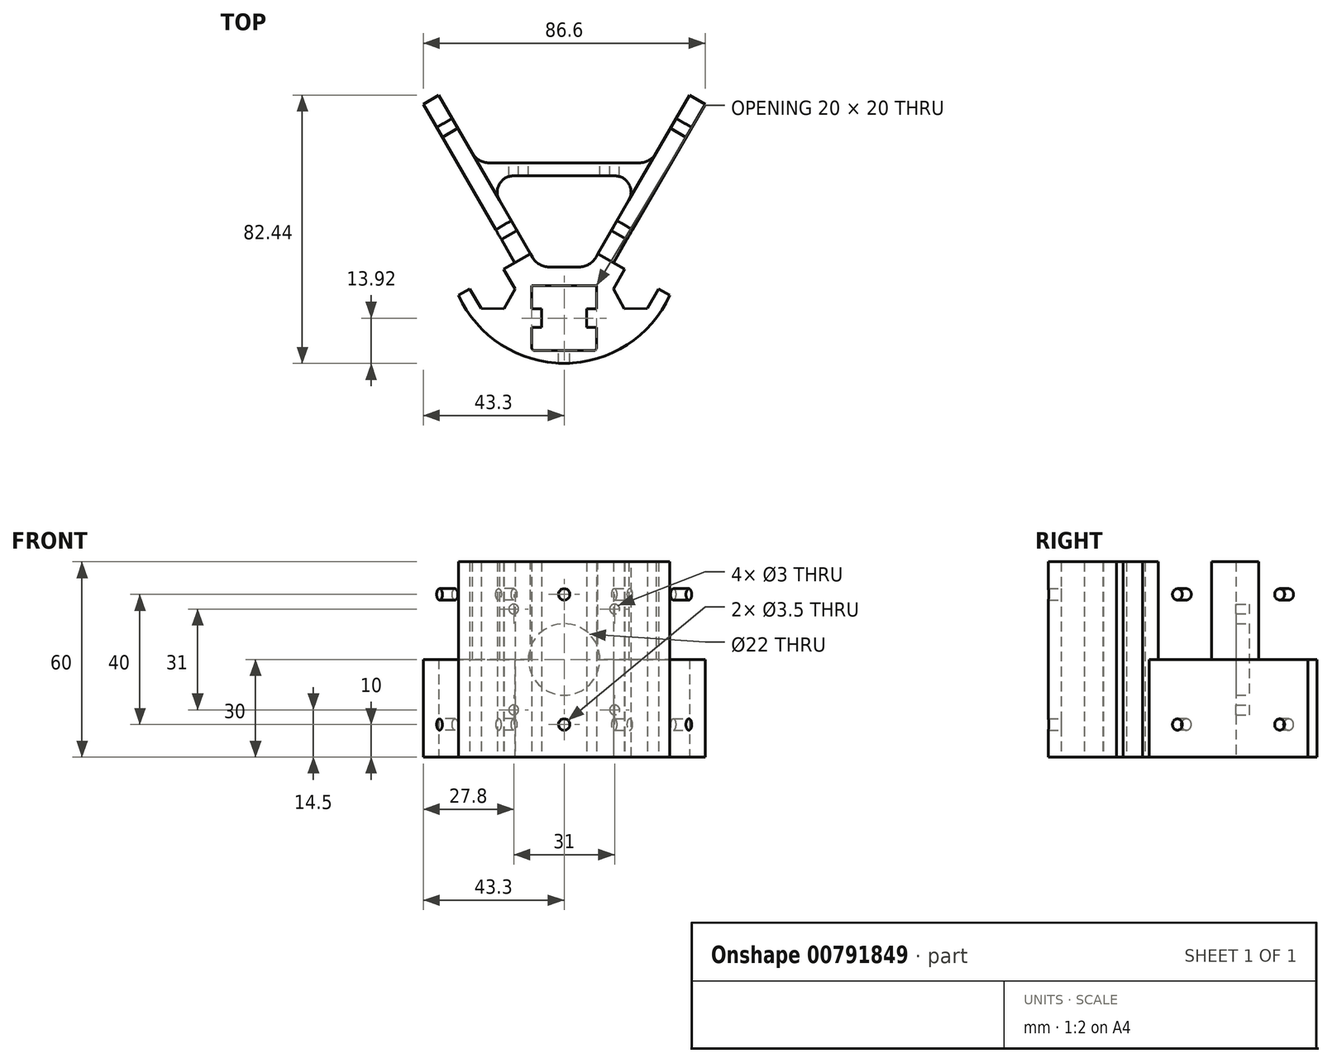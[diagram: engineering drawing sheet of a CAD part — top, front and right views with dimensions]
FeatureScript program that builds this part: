
annotation { "Feature Type Name" : "Feature", "Feature Type Description" : "" }
export const myFeature = defineFeature(function(context is Context, id is Id, definition is map)
    precondition{}
    {
        {
            var Q0;
            Q0=qCreatedBy(makeId("Top.planeOp"),FACE);
            var sketch = newSketch(context, id + "F0", { "sketchPlane" : qUnion([Q0])});
            skLineSegment(sketch, "E0", {"start": v(0, 0) * mm, "end": v(32.48, 0) * mm});
            skLineSegment(sketch, "E1", {"start": v(0, 0) * mm, "end": v(-32.48, 0) * mm});
            skArc(sketch, "E2", {"start": v(-32.48, 0) * mm, "mid": v(0, -20.94) * mm, "end": v(32.48, 0) * mm});
            skLineSegment(sketch, "E3", {"start": v(-32.48, 0) * mm, "end": v(-15.15, 10) * mm});
            skLineSegment(sketch, "E4", {"start": v(32.48, 0) * mm, "end": v(15.15, 10) * mm});
            skLineSegment(sketch, "E5", {"start": v(15.15, 10) * mm, "end": v(43.3, 58.75) * mm});
            skLineSegment(sketch, "E6", {"start": v(-15.15, 10) * mm, "end": v(-43.3, 58.75) * mm});
            skLineSegment(sketch, "E7", {"start": v(38.54, 61.5) * mm, "end": v(43.3, 58.75) * mm});
            skLineSegment(sketch, "E8.bottom", {"start": v(10, -17.02) * mm, "end": v(-10, -17.02) * mm});
            skLineSegment(sketch, "E8.top", {"start": v(10, 2.98) * mm, "end": v(-10, 2.98) * mm});
            skLineSegment(sketch, "E8.left", {"start": v(10, -17.02) * mm, "end": v(10, 2.98) * mm});
            skLineSegment(sketch, "E8.right", {"start": v(-10, -17.02) * mm, "end": v(-10, 2.98) * mm});
            skPoint(sketch, "E8.middle", {"position": v(0, -7.02) * mm});
            skLineSegment(sketch, "E9", {"start": v(-64.62, 8.7) * mm, "end": v(74.38, 8.7) * mm});
            skLineSegment(sketch, "E10", {"start": v(-43.3, 58.75) * mm, "end": v(-38.54, 61.5) * mm});
            skLineSegment(sketch, "E11", {"start": v(-38.54, 61.5) * mm, "end": v(-8.06, 8.7) * mm});
            skLineSegment(sketch, "E12", {"start": v(38.54, 61.5) * mm, "end": v(8.06, 8.7) * mm});
            skLineSegment(sketch, "E13", {"start": v(-64.62, 36.7) * mm, "end": v(67.86, 36.7) * mm});
            skLineSegment(sketch, "E14", {"start": v(-64.87, 40.7) * mm, "end": v(70.08, 40.7) * mm});
            skLineSegment(sketch, "E15.bottom", {"start": v(-10, -7.02) * mm, "end": v(-6.9, -7.02) * mm});
            skLineSegment(sketch, "E15.top", {"start": v(-10, -4.12) * mm, "end": v(-6.9, -4.12) * mm});
            skLineSegment(sketch, "E15.left", {"start": v(-10, -7.02) * mm, "end": v(-10, -4.12) * mm});
            skLineSegment(sketch, "E15.right", {"start": v(-6.9, -7.02) * mm, "end": v(-6.9, -4.12) * mm});
            skLineSegment(sketch, "E16.top", {"start": v(-10, -9.92) * mm, "end": v(-6.9, -9.92) * mm});
            skLineSegment(sketch, "E16.left", {"start": v(-10, -7.02) * mm, "end": v(-10, -9.92) * mm});
            skLineSegment(sketch, "E16.right", {"start": v(-6.9, -7.02) * mm, "end": v(-6.9, -9.92) * mm});
            skLineSegment(sketch, "E17.1.0", {"start": v(10, 2.98) * mm, "end": v(10, -17.02) * mm});
            skLineSegment(sketch, "E17.1.1", {"start": v(2.9, -17.02) * mm, "end": v(2.9, -13.92) * mm});
            skLineSegment(sketch, "E17.1.2", {"start": v(0, -17.02) * mm, "end": v(0, -13.92) * mm});
            skLineSegment(sketch, "E17.1.3", {"start": v(-2.9, -17.02) * mm, "end": v(-2.9, -13.92) * mm});
            skLineSegment(sketch, "E17.1.4", {"start": v(0, -13.92) * mm, "end": v(-2.9, -13.92) * mm});
            skLineSegment(sketch, "E17.1.5", {"start": v(0, -13.92) * mm, "end": v(2.9, -13.92) * mm});
            skLineSegment(sketch, "E17.2.0", {"start": v(-10, 2.98) * mm, "end": v(10, 2.98) * mm});
            skLineSegment(sketch, "E17.2.1", {"start": v(10, -4.12) * mm, "end": v(6.9, -4.12) * mm});
            skLineSegment(sketch, "E17.2.2", {"start": v(10, -7.02) * mm, "end": v(6.9, -7.02) * mm});
            skLineSegment(sketch, "E17.2.3", {"start": v(10, -9.92) * mm, "end": v(6.9, -9.92) * mm});
            skLineSegment(sketch, "E17.2.4", {"start": v(6.9, -7.02) * mm, "end": v(6.9, -9.92) * mm});
            skLineSegment(sketch, "E17.2.5", {"start": v(6.9, -7.02) * mm, "end": v(6.9, -4.12) * mm});
            skLineSegment(sketch, "E17.3.1", {"start": v(-2.9, 2.98) * mm, "end": v(-2.9, -0.12) * mm});
            skLineSegment(sketch, "E17.3.2", {"start": v(0, 2.98) * mm, "end": v(0, -0.12) * mm});
            skLineSegment(sketch, "E17.3.3", {"start": v(2.9, 2.98) * mm, "end": v(2.9, -0.12) * mm});
            skLineSegment(sketch, "E17.3.4", {"start": v(0, -0.12) * mm, "end": v(2.9, -0.12) * mm});
            skLineSegment(sketch, "E17.3.5", {"start": v(0, -0.12) * mm, "end": v(-2.9, -0.12) * mm});
            skLineSegment(sketch, "E18", {"start": v(18.62, 8) * mm, "end": v(15.12, 1.94) * mm});
            skLineSegment(sketch, "E19", {"start": v(29.01, 2) * mm, "end": v(25.51, -4.06) * mm});
            skPoint(sketch, "E20", {"position": v(23.81, 5) * mm});
            skLineSegment(sketch, "E21", {"start": v(15.12, 1.94) * mm, "end": v(18.51, -4.18) * mm});
            skLineSegment(sketch, "E22", {"start": v(25.51, -4.06) * mm, "end": v(18.51, -4.18) * mm});
            skLineSegment(sketch, "E23.MirrorCS", {"start": v(-18.62, 8) * mm, "end": v(-15.12, 1.94) * mm});
            skLineSegment(sketch, "E24.MirrorCS", {"start": v(-15.12, 1.94) * mm, "end": v(-18.51, -4.18) * mm});
            skLineSegment(sketch, "E25.MirrorCS", {"start": v(-25.51, -4.06) * mm, "end": v(-18.51, -4.18) * mm});
            skLineSegment(sketch, "E26.MirrorCS", {"start": v(-29.01, 2) * mm, "end": v(-25.51, -4.06) * mm});
            skSolve(sketch);
        }
        {
            var Q0;
            {var subQ0=sQuery(id+"F0.wireOp",EDGE,"E2");Q0=makeQuery(id+"F0.imprint","IMPRINT",FACE,{"disambiguationData":[TD([[makeQuery(id+"F0.imprint","IMPRINT",EDGE,{"derivedFrom":subQ0}),1.0]])]});}
            var Q1;
            {var subQ16=sQuery(id+"F0.wireOp",EDGE,"E8.top");Q1=makeQuery(id+"F0.imprint","IMPRINT",FACE,{"disambiguationData":[TD([[makeQuery(id+"F0.imprint","IMPRINT",EDGE,{"derivedFrom":subQ16}),-1.0]])]});}
            var Q2;
            {var subQ5=sQuery(id+"F0.wireOp",EDGE,"E5");var subQ6=sQuery(id+"F0.wireOp",EDGE,"E4");var subQ7=makeQuery(id+"F0.imprint","INTERSECT",VERTEX,{"derivedFrom":[subQ6,subQ5]});Q2=makeQuery(id+"F0.imprint","IMPRINT",FACE,{"disambiguationData":[TD([[makeQuery(id+"F0.imprint","IMPRINT",EDGE,{"disambiguationData":[TD([[subQ7,1.0]])],"derivedFrom":subQ6}),1.0]])]});}
            var Q3;
            {var subQ5=sQuery(id+"F0.wireOp",EDGE,"E6");var subQ6=sQuery(id+"F0.wireOp",EDGE,"E3");var subQ7=makeQuery(id+"F0.imprint","INTERSECT",VERTEX,{"derivedFrom":[subQ6,subQ5]});Q3=makeQuery(id+"F0.imprint","IMPRINT",FACE,{"disambiguationData":[TD([[makeQuery(id+"F0.imprint","IMPRINT",EDGE,{"disambiguationData":[TD([[subQ7,1.0]])],"derivedFrom":subQ6}),-1.0]])]});}
            var Q4;
            {var subQ0=sQuery(id+"F0.wireOp",EDGE,"E10");Q4=makeQuery(id+"F0.imprint","IMPRINT",FACE,{"disambiguationData":[TD([[makeQuery(id+"F0.imprint","IMPRINT",EDGE,{"derivedFrom":subQ0}),-1.0]])]});}
            var Q5;
            {var subQ0=sQuery(id+"F0.wireOp",EDGE,"E7");Q5=makeQuery(id+"F0.imprint","IMPRINT",FACE,{"disambiguationData":[TD([[makeQuery(id+"F0.imprint","IMPRINT",EDGE,{"derivedFrom":subQ0}),-1.0]])]});}
            var Q6;
            {var subQ0=sQuery(id+"F0.wireOp",EDGE,"E13");var subQ1=sQuery(id+"F0.wireOp",EDGE,"E5");var subQ2=makeQuery(id+"F0.imprint","INTERSECT",VERTEX,{"derivedFrom":[subQ1,subQ0]});Q6=makeQuery(id+"F0.imprint","IMPRINT",FACE,{"disambiguationData":[TD([[makeQuery(id+"F0.imprint","IMPRINT",EDGE,{"disambiguationData":[TD([[subQ2,-1.0]])],"derivedFrom":subQ1}),1.0]])]});}
            var Q7;
            {var subQ0=sQuery(id+"F0.wireOp",EDGE,"E14");var subQ1=sQuery(id+"F0.wireOp",EDGE,"E11");var subQ2=makeQuery(id+"F0.imprint","INTERSECT",VERTEX,{"derivedFrom":[subQ1,subQ0]});Q7=makeQuery(id+"F0.imprint","IMPRINT",FACE,{"disambiguationData":[TD([[makeQuery(id+"F0.imprint","IMPRINT",EDGE,{"disambiguationData":[TD([[subQ2,-1.0]])],"derivedFrom":subQ1}),1.0]])]});}
            var Q8;
            {var subQ0=sQuery(id+"F0.wireOp",EDGE,"E13");var subQ1=sQuery(id+"F0.wireOp",EDGE,"E6");var subQ2=makeQuery(id+"F0.imprint","INTERSECT",VERTEX,{"derivedFrom":[subQ1,subQ0]});Q8=makeQuery(id+"F0.imprint","IMPRINT",FACE,{"disambiguationData":[TD([[makeQuery(id+"F0.imprint","IMPRINT",EDGE,{"disambiguationData":[TD([[subQ2,-1.0]])],"derivedFrom":subQ1}),-1.0]])]});}
            var Q9;
            {var subQ11=sQuery(id+"F0.wireOp",EDGE,"E9");var subQ12=makeQuery(id+"F0.imprint","INTERSECT",VERTEX,{"derivedFrom":[subQ11,sQuery(id+"F0.wireOp",EDGE,"E11")]});Q9=makeQuery(id+"F0.imprint","IMPRINT",FACE,{"disambiguationData":[TD([[makeQuery(id+"F0.imprint","IMPRINT",EDGE,{"disambiguationData":[TD([[subQ12,1.0]])],"derivedFrom":subQ11}),-1.0]])]});}
            var Q10;
            {var subQ0=sQuery(id+"F0.wireOp",EDGE,"E17.3.2");var subQ5=sQuery(id+"F0.wireOp",EDGE,"E17.2.0");var subQ6=makeQuery(id+"F0.imprint","INTERSECT",VERTEX,{"derivedFrom":[subQ5,subQ0]});Q10=makeQuery(id+"F0.imprint","IMPRINT",FACE,{"disambiguationData":[TD([[makeQuery(id+"F0.imprint","IMPRINT",EDGE,{"disambiguationData":[TD([[subQ6,-1.0]])],"derivedFrom":subQ5}),-1.0]])]});}
            var Q11;
            {var subQ3=sQuery(id+"F0.wireOp",EDGE,"E17.3.1");var subQ5=sQuery(id+"F0.wireOp",EDGE,"E17.2.0");var subQ6=makeQuery(id+"F0.imprint","INTERSECT",VERTEX,{"derivedFrom":[subQ5,subQ3]});Q11=makeQuery(id+"F0.imprint","IMPRINT",FACE,{"disambiguationData":[TD([[makeQuery(id+"F0.imprint","IMPRINT",EDGE,{"disambiguationData":[TD([[subQ6,-1.0]])],"derivedFrom":subQ5}),-1.0]])]});}
            var Q12;
            {var subQ0=sQuery(id+"F0.wireOp",EDGE,"E15.bottom");Q12=makeQuery(id+"F0.imprint","IMPRINT",FACE,{"disambiguationData":[TD([[makeQuery(id+"F0.imprint","IMPRINT",EDGE,{"derivedFrom":subQ0}),-1.0]])]});}
            var Q13;
            {var subQ0=sQuery(id+"F0.wireOp",EDGE,"E15.top");Q13=makeQuery(id+"F0.imprint","IMPRINT",FACE,{"disambiguationData":[TD([[makeQuery(id+"F0.imprint","IMPRINT",EDGE,{"derivedFrom":subQ0}),-1.0]])]});}
            var Q14;
            {var subQ0=sQuery(id+"F0.wireOp",EDGE,"E17.2.1");Q14=makeQuery(id+"F0.imprint","IMPRINT",FACE,{"disambiguationData":[TD([[makeQuery(id+"F0.imprint","IMPRINT",EDGE,{"derivedFrom":subQ0}),1.0]])]});}
            var Q15;
            {var subQ0=sQuery(id+"F0.wireOp",EDGE,"E17.2.2");Q15=makeQuery(id+"F0.imprint","IMPRINT",FACE,{"disambiguationData":[TD([[makeQuery(id+"F0.imprint","IMPRINT",EDGE,{"derivedFrom":subQ0}),1.0]])]});}
            var Q16;
            {var subQ0=sQuery(id+"F0.wireOp",EDGE,"E3");var subQ3=sQuery(id+"F0.wireOp",EDGE,"E26.MirrorCS");var subQ5=makeQuery(id+"F0.imprint","INTERSECT",VERTEX,{"derivedFrom":[subQ0,subQ3]});Q16=makeQuery(id+"F0.imprint","IMPRINT",FACE,{"disambiguationData":[TD([[makeQuery(id+"F0.imprint","IMPRINT",EDGE,{"disambiguationData":[TD([[subQ5,-1.0]])],"derivedFrom":subQ3}),-1.0]])]});}
            var Q17;
            {var subQ0=sQuery(id+"F0.wireOp",EDGE,"E4");var subQ3=sQuery(id+"F0.wireOp",EDGE,"E19");var subQ5=makeQuery(id+"F0.imprint","INTERSECT",VERTEX,{"derivedFrom":[subQ0,subQ3]});Q17=makeQuery(id+"F0.imprint","IMPRINT",FACE,{"disambiguationData":[TD([[makeQuery(id+"F0.imprint","IMPRINT",EDGE,{"disambiguationData":[TD([[subQ5,-1.0]])],"derivedFrom":subQ3}),1.0]])]});}
            extrude(context, id + "F1", {"entities" : qUnion([Q0, Q1, Q2, Q3, Q4, Q5, Q6, Q7, Q8, Q9, Q10, Q11, Q12, Q13, Q14, Q15, Q16, Q17]), "depth" : 60 * mm});
        }
        {
            var Q0;
            Q0=makeQuery(id+"F1.opExtrude","SWEPT_EDGE",EDGE,{"disambiguationData":[OSD([sQuery(id+"F0.wireOp",EDGE,"E9"),sQuery(id+"F0.wireOp",EDGE,"E11")])]});
            var Q1;
            Q1=makeQuery(id+"F1.opExtrude","SWEPT_EDGE",EDGE,{"disambiguationData":[OSD([sQuery(id+"F0.wireOp",EDGE,"E9"),sQuery(id+"F0.wireOp",EDGE,"E12")])]});
            var Q2;
            Q2=makeQuery(id+"F1.opExtrude","SWEPT_EDGE",EDGE,{"disambiguationData":[OSD([sQuery(id+"F0.wireOp",EDGE,"E12"),sQuery(id+"F0.wireOp",EDGE,"E14")])]});
            var Q3;
            Q3=makeQuery(id+"F1.opExtrude","SWEPT_EDGE",EDGE,{"disambiguationData":[OSD([sQuery(id+"F0.wireOp",EDGE,"E11"),sQuery(id+"F0.wireOp",EDGE,"E14")])]});
            fillet(context, id + "F2", {"entities" : qUnion([Q0, Q1, Q2, Q3]), "radius" : 6 * mm, "tangentPropagation" : true, "allowEdgeOverflow" : false});
        }
        {
            var Q0;
            Q0=makeQuery(id+"F1.opExtrude","SWEPT_EDGE",EDGE,{"disambiguationData":[OSD([sQuery(id+"F0.wireOp",EDGE,"E8.bottom"),sQuery(id+"F0.wireOp",EDGE,"E8.right")])]});
            var Q1;
            Q1=makeQuery(id+"F1.opExtrude","SWEPT_EDGE",EDGE,{"disambiguationData":[OSD([sQuery(id+"F0.wireOp",EDGE,"E8.bottom"),sQuery(id+"F0.wireOp",EDGE,"E17.1.0")])]});
            var Q2;
            Q2=makeQuery(id+"F1.opExtrude","SWEPT_EDGE",EDGE,{"disambiguationData":[OSD([sQuery(id+"F0.wireOp",EDGE,"E17.1.0"),sQuery(id+"F0.wireOp",EDGE,"E17.2.0")])]});
            var Q3;
            Q3=makeQuery(id+"F1.opExtrude","SWEPT_EDGE",EDGE,{"disambiguationData":[OSD([sQuery(id+"F0.wireOp",EDGE,"E17.2.0"),sQuery(id+"F0.wireOp",EDGE,"E8.right")])]});
            fillet(context, id + "F3", {"entities" : qUnion([Q0, Q1, Q2, Q3]), "radius" : 1 * mm, "tangentPropagation" : true, "allowEdgeOverflow" : false});
        }
        {
            var Q0;
            Q0=makeQuery(id+"F1.opExtrude","SWEPT_EDGE",EDGE,{"disambiguationData":[OSD([sQuery(id+"F0.wireOp",EDGE,"E11"),sQuery(id+"F0.wireOp",EDGE,"E13")])]});
            var Q1;
            Q1=makeQuery(id+"F1.opExtrude","SWEPT_EDGE",EDGE,{"disambiguationData":[OSD([sQuery(id+"F0.wireOp",EDGE,"E12"),sQuery(id+"F0.wireOp",EDGE,"E13")])]});
            fillet(context, id + "F4", {"entities" : qUnion([Q0, Q1]), "radius" : 5 * mm, "tangentPropagation" : true, "allowEdgeOverflow" : false});
        }
        {
            var Q0;
            Q0=makeQuery(id+"F1.opExtrude","SWEPT_FACE",FACE,{"disambiguationData":[OSD([sQuery(id+"F0.wireOp",EDGE,"E5")])]});
            var sketch = newSketch(context, id + "F5", { "sketchPlane" : qUnion([Q0])});
            skCircle(sketch, "E27", {"center": v(26.24, 10) * mm, "radius": 1.75 * mm});
            skCircle(sketch, "E28", {"center": v(62.53, 10) * mm, "radius": 1.75 * mm});
            skLineSegment(sketch, "E29", {"start": v(16.24, 30) * mm, "end": v(72.53, 30) * mm});
            skCircle(sketch, "E30.MirrorC", {"center": v(26.24, 50) * mm, "radius": 1.75 * mm});
            skCircle(sketch, "E31.MirrorC", {"center": v(62.53, 50) * mm, "radius": 1.75 * mm});
            skSolve(sketch);
        }
        {
            var Q0;
            Q0=makeQuery(id+"F5.imprint","IMPRINT",FACE,{"disambiguationData":[TD([[makeQuery(id+"F5.imprint","IMPRINT",EDGE,{"derivedFrom":sQuery(id+"F5.wireOp",EDGE,"E30.MirrorC")}),-1.0]])]});
            var Q1;
            Q1=makeQuery(id+"F5.imprint","IMPRINT",FACE,{"disambiguationData":[TD([[makeQuery(id+"F5.imprint","IMPRINT",EDGE,{"derivedFrom":sQuery(id+"F5.wireOp",EDGE,"E31.MirrorC")}),-1.0]])]});
            var Q2;
            Q2=makeQuery(id+"F5.imprint","IMPRINT",FACE,{"disambiguationData":[TD([[makeQuery(id+"F5.imprint","IMPRINT",EDGE,{"derivedFrom":sQuery(id+"F5.wireOp",EDGE,"E27")}),1.0]])]});
            var Q3;
            Q3=makeQuery(id+"F5.imprint","IMPRINT",FACE,{"disambiguationData":[TD([[makeQuery(id+"F5.imprint","IMPRINT",EDGE,{"derivedFrom":sQuery(id+"F5.wireOp",EDGE,"E28")}),1.0]])]});
            var Q4;
            {var subQ0=sQuery(id+"F0.wireOp",EDGE,"E12");Q4=makeQuery(id+"F1.opExtrude","SWEPT_FACE",FACE,{"disambiguationData":[OSD([subQ0]),TDD([makeQuery(id+"F0.imprint","IMPRINT",EDGE,{"disambiguationData":[TD([[makeQuery(id+"F0.imprint","INTERSECT",VERTEX,{"derivedFrom":[sQuery(id+"F0.wireOp",EDGE,"E9"),subQ0]}),1.0]])],"derivedFrom":subQ0})])]});}
            extrude(context, id + "F6", {"entities" : qUnion([Q0, Q1, Q2, Q3]), "operationType" : NewBodyOperationType.REMOVE, "endBound" : BoundingType.UP_TO_SURFACE, "oppositeDirection" : true, "endBoundEntityFace" : qUnion([Q4]), "depth" : 25 * mm});
        }
        {
            var Q0;
            Q0=makeQuery(id+"F1.opExtrude","SWEPT_FACE",FACE,{"disambiguationData":[OSD([sQuery(id+"F0.wireOp",EDGE,"E8.bottom")])]});
            var sketch = newSketch(context, id + "F7", { "sketchPlane" : qUnion([Q0])});
            skCircle(sketch, "E32", {"center": v(0, 50) * mm, "radius": 1.75 * mm});
            skPoint(sketch, "E32.centerSnap0", {"position": v(0, 60) * mm});
            skCircle(sketch, "E33", {"center": v(0, 10) * mm, "radius": 1.75 * mm});
            skSolve(sketch);
        }
        {
            var Q0;
            Q0=qSketchRegion(id+"F7",true);
            var Q1;
            Q1=makeQuery(id+"F1.opExtrude","SWEPT_FACE",FACE,{"disambiguationData":[OSD([sQuery(id+"F0.wireOp",EDGE,"E2")])]});
            extrude(context, id + "F8", {"entities" : qUnion([Q0]), "operationType" : NewBodyOperationType.REMOVE, "endBound" : BoundingType.UP_TO_SURFACE, "oppositeDirection" : true, "endBoundEntityFace" : qUnion([Q1]), "depth" : 25 * mm});
        }
        {
            var Q0;
            Q0=makeQuery(id+"F1.opExtrude","SWEPT_BODY",BODY,{"disambiguationData":[OSD([sQuery(id+"F0.wireOp",EDGE,"E0"),sQuery(id+"F0.wireOp",EDGE,"E1"),sQuery(id+"F0.wireOp",EDGE,"E2"),sQuery(id+"F0.wireOp",EDGE,"E3"),sQuery(id+"F0.wireOp",EDGE,"E4"),sQuery(id+"F0.wireOp",EDGE,"E5"),sQuery(id+"F0.wireOp",EDGE,"E6"),sQuery(id+"F0.wireOp",EDGE,"E7"),sQuery(id+"F0.wireOp",EDGE,"E8.bottom"),sQuery(id+"F0.wireOp",EDGE,"E9"),sQuery(id+"F0.wireOp",EDGE,"E10"),sQuery(id+"F0.wireOp",EDGE,"E11"),sQuery(id+"F0.wireOp",EDGE,"E12"),sQuery(id+"F0.wireOp",EDGE,"E13"),sQuery(id+"F0.wireOp",EDGE,"E14"),sQuery(id+"F0.wireOp",EDGE,"E15.top"),sQuery(id+"F0.wireOp",EDGE,"E15.right"),sQuery(id+"F0.wireOp",EDGE,"E16.top"),sQuery(id+"F0.wireOp",EDGE,"E16.right"),sQuery(id+"F0.wireOp",EDGE,"E17.1.0"),sQuery(id+"F0.wireOp",EDGE,"E17.2.0"),sQuery(id+"F0.wireOp",EDGE,"E17.2.1"),sQuery(id+"F0.wireOp",EDGE,"E17.2.3"),sQuery(id+"F0.wireOp",EDGE,"E17.2.4"),sQuery(id+"F0.wireOp",EDGE,"E17.2.5"),sQuery(id+"F0.wireOp",EDGE,"E8.right"),sQuery(id+"F0.wireOp",EDGE,"E17.3.1"),sQuery(id+"F0.wireOp",EDGE,"E17.3.3"),sQuery(id+"F0.wireOp",EDGE,"E18"),sQuery(id+"F0.wireOp",EDGE,"E19"),sQuery(id+"F0.wireOp",EDGE,"E21"),sQuery(id+"F0.wireOp",EDGE,"E22"),sQuery(id+"F0.wireOp",EDGE,"E23.MirrorCS"),sQuery(id+"F0.wireOp",EDGE,"E24.MirrorCS"),sQuery(id+"F0.wireOp",EDGE,"E25.MirrorCS"),sQuery(id+"F0.wireOp",EDGE,"E26.MirrorCS")])]});
            transform(context, id + "F9", {"entities" : qUnion([Q0]), "transformType" : TransformType.TRANSLATION_3D, "dx" : 0 * mm, "dy" : 7.02 * mm, "dz" : 0 * mm, "makeCopy" : false});
        }
        {
            var Q0;
            Q0=makeQuery(id+"F1.opExtrude","SWEPT_FACE",FACE,{"disambiguationData":[OSD([sQuery(id+"F0.wireOp",EDGE,"E14")])]});
            var sketch = newSketch(context, id + "F10", { "sketchPlane" : qUnion([Q0])});
            skCircle(sketch, "E34", {"center": v(0, 30) * mm, "radius": 11 * mm});
            skCircle(sketch, "E35", {"center": v(-15.5, 45.5) * mm, "radius": 1.5 * mm});
            skCircle(sketch, "E36", {"center": v(-15.5, 14.5) * mm, "radius": 1.5 * mm});
            skSolve(sketch);
        }
        {
            var Q0;
            Q0=makeQuery(id+"F10.imprint","IMPRINT",FACE,{"disambiguationData":[TD([[makeQuery(id+"F10.imprint","IMPRINT",EDGE,{"derivedFrom":sQuery(id+"F10.wireOp",EDGE,"E34")}),1.0]])]});
            var Q1;
            Q1=makeQuery(id+"F10.imprint","IMPRINT",FACE,{"disambiguationData":[TD([[makeQuery(id+"F10.imprint","IMPRINT",EDGE,{"derivedFrom":sQuery(id+"F10.wireOp",EDGE,"E35")}),1.0]])]});
            var Q2;
            Q2=makeQuery(id+"F10.imprint","IMPRINT",FACE,{"disambiguationData":[TD([[makeQuery(id+"F10.imprint","IMPRINT",EDGE,{"derivedFrom":sQuery(id+"F10.wireOp",EDGE,"E36")}),1.0]])]});
            var Q3;
            Q3=makeQuery(id+"F1.opExtrude","SWEPT_FACE",FACE,{"disambiguationData":[OSD([sQuery(id+"F0.wireOp",EDGE,"E13")])]});
            extrude(context, id + "F11", {"entities" : qUnion([Q0, Q1, Q2]), "operationType" : NewBodyOperationType.REMOVE, "oppositeDirection" : true, "endBoundEntityFace" : qUnion([Q3]), "depth" : 10 * mm});
        }
        {
            var Q0;
            Q0=makeQuery(id+"F1.opExtrude","SWEPT_BODY",BODY,{"disambiguationData":[OSD([sQuery(id+"F0.wireOp",EDGE,"E0"),sQuery(id+"F0.wireOp",EDGE,"E1"),sQuery(id+"F0.wireOp",EDGE,"E2"),sQuery(id+"F0.wireOp",EDGE,"E3"),sQuery(id+"F0.wireOp",EDGE,"E4"),sQuery(id+"F0.wireOp",EDGE,"E5"),sQuery(id+"F0.wireOp",EDGE,"E6"),sQuery(id+"F0.wireOp",EDGE,"E7"),sQuery(id+"F0.wireOp",EDGE,"E8.bottom"),sQuery(id+"F0.wireOp",EDGE,"E9"),sQuery(id+"F0.wireOp",EDGE,"E10"),sQuery(id+"F0.wireOp",EDGE,"E11"),sQuery(id+"F0.wireOp",EDGE,"E12"),sQuery(id+"F0.wireOp",EDGE,"E13"),sQuery(id+"F0.wireOp",EDGE,"E14"),sQuery(id+"F0.wireOp",EDGE,"E15.top"),sQuery(id+"F0.wireOp",EDGE,"E15.right"),sQuery(id+"F0.wireOp",EDGE,"E16.top"),sQuery(id+"F0.wireOp",EDGE,"E16.right"),sQuery(id+"F0.wireOp",EDGE,"E17.1.0"),sQuery(id+"F0.wireOp",EDGE,"E17.2.0"),sQuery(id+"F0.wireOp",EDGE,"E17.2.1"),sQuery(id+"F0.wireOp",EDGE,"E17.2.3"),sQuery(id+"F0.wireOp",EDGE,"E17.2.4"),sQuery(id+"F0.wireOp",EDGE,"E17.2.5"),sQuery(id+"F0.wireOp",EDGE,"E8.right"),sQuery(id+"F0.wireOp",EDGE,"E17.3.1"),sQuery(id+"F0.wireOp",EDGE,"E17.3.3"),sQuery(id+"F0.wireOp",EDGE,"E18"),sQuery(id+"F0.wireOp",EDGE,"E19"),sQuery(id+"F0.wireOp",EDGE,"E21"),sQuery(id+"F0.wireOp",EDGE,"E22"),sQuery(id+"F0.wireOp",EDGE,"E23.MirrorCS"),sQuery(id+"F0.wireOp",EDGE,"E24.MirrorCS"),sQuery(id+"F0.wireOp",EDGE,"E25.MirrorCS"),sQuery(id+"F0.wireOp",EDGE,"E26.MirrorCS")])]});
            var Q1;
            Q1=qCreatedBy(makeId("Right.planeOp"),FACE);
            mirror(context, id + "F12", {"operationType" : NewBodyOperationType.INTERSECT, "entities" : qUnion([Q0]), "mirrorPlane" : qUnion([Q1])});
        }
    });
